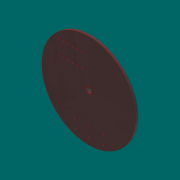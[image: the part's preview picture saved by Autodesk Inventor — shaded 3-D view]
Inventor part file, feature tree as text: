
AUTODESK INVENTOR PART (.ipt)
format: ipt  version: 2013 (Build 170138000, 138)  size: 138,752 bytes
history: native  units: mm
features: sketch x4, extrude x2, hole x2, other x1
ambient origin geometry x8: Origin, YZ Plane, XZ Plane, XY Plane, X Axis, Y Axis, Z Axis, Center Point
feature tree (9):
  other  "ソリッド1"
  extrude  "押し出し1"  Depth=200.0mm
  hole  "穴5"  [1 undecoded]
  extrude  "押し出し4"  Depth=7.0mm
  hole  "穴6"  [1 undecoded]
  sketch  "スケッチ1"
  sketch  "スケッチ12"
  sketch  "スケッチ13"
  sketch  "スケッチ14"
note: 2 required parameter values undecoded (feature->parameter linkage not recoverable at this tier; creation-order binding heuristic only, values carry confidence <= 0.55)
